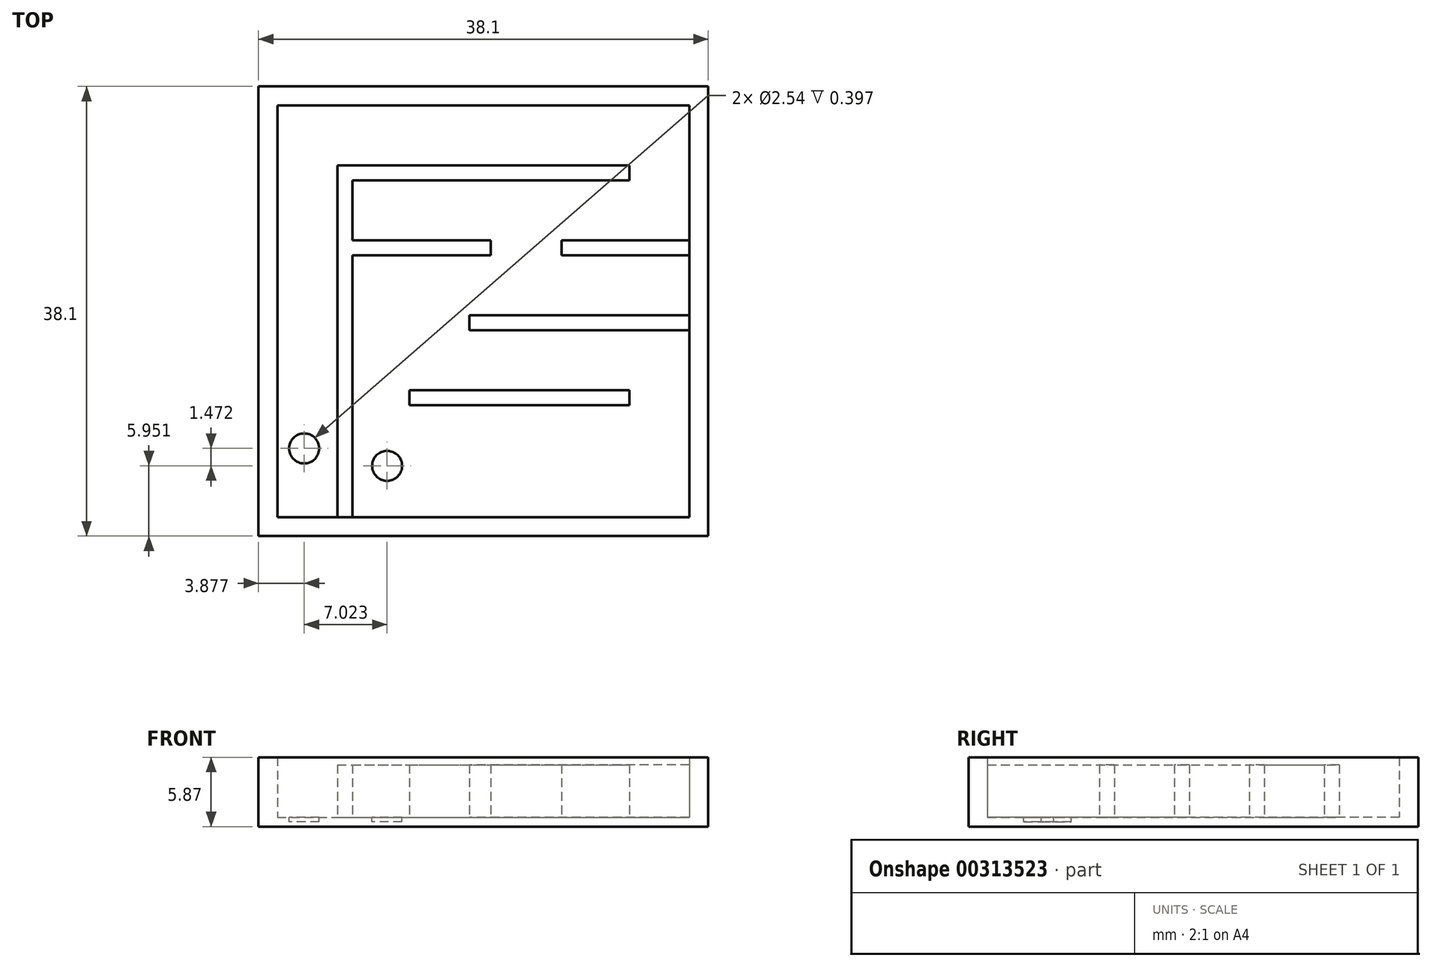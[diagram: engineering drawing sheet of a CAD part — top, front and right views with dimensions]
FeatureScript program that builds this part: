
annotation { "Feature Type Name" : "Feature", "Feature Type Description" : "" }
export const myFeature = defineFeature(function(context is Context, id is Id, definition is map)
    precondition{}
    {
        {
            var Q0;
            Q0=qCreatedBy(makeId("Top.planeOp"),FACE);
            var sketch = newSketch(context, id + "F0", { "sketchPlane" : qUnion([Q0])});
            skLineSegment(sketch, "E0.bottom", {"start": v(-58.63, 60.9) * mm, "end": v(-20.53, 60.9) * mm});
            skLineSegment(sketch, "E0.top", {"start": v(-58.63, 22.8) * mm, "end": v(-20.53, 22.8) * mm});
            skLineSegment(sketch, "E0.left", {"start": v(-58.63, 60.9) * mm, "end": v(-58.63, 22.8) * mm});
            skLineSegment(sketch, "E0.right", {"start": v(-20.53, 60.9) * mm, "end": v(-20.53, 22.8) * mm});
            skSolve(sketch);
        }
        {
            var Q0;
            Q0=makeQuery(id+"F0.imprint","IMPRINT",FACE,{"disambiguationData":[TD([[makeQuery(id+"F0.imprint","IMPRINT",EDGE,{"derivedFrom":sQuery(id+"F0.wireOp",EDGE,"E0.bottom")}),-1.0]])]});
            extrude(context, id + "F1", {"entities" : qUnion([Q0]), "depth" : 0.8 * mm});
        }
        {
            var Q0;
            Q0=makeQuery(id+"F1.opExtrude","CAP_FACE",FACE,{"disambiguationData":[OSD([sQuery(id+"F0.wireOp",EDGE,"E0.bottom"),sQuery(id+"F0.wireOp",EDGE,"E0.top"),sQuery(id+"F0.wireOp",EDGE,"E0.left"),sQuery(id+"F0.wireOp",EDGE,"E0.right")])],"isStart":false});
            var sketch = newSketch(context, id + "F2", { "sketchPlane" : qUnion([Q0])});
            skLineSegment(sketch, "E1.0", {"start": v(-57.03, 59.3) * mm, "end": v(-22.13, 59.3) * mm});
            skLineSegment(sketch, "E1.1", {"start": v(-57.03, 59.3) * mm, "end": v(-57.03, 24.4) * mm});
            skLineSegment(sketch, "E1.2", {"start": v(-57.03, 24.4) * mm, "end": v(-22.13, 24.4) * mm});
            skLineSegment(sketch, "E1.3", {"start": v(-22.13, 59.3) * mm, "end": v(-22.13, 24.4) * mm});
            skSolve(sketch);
        }
        {
            var Q0;
            Q0=makeQuery(id+"F2.imprint","IMPRINT",FACE,{"disambiguationData":[TD([[makeQuery(id+"F2.imprint","IMPRINT",EDGE,{"derivedFrom":sQuery(id+"F2.wireOp",EDGE,"E1.0")}),1.0]])]});
            extrude(context, id + "F3", {"entities" : qUnion([Q0]), "operationType" : NewBodyOperationType.ADD, "depth" : 5.08 * mm});
        }
        {
            var Q0;
            Q0=makeQuery(id+"F1.opExtrude","CAP_FACE",FACE,{"disambiguationData":[OSD([sQuery(id+"F0.wireOp",EDGE,"E0.bottom"),sQuery(id+"F0.wireOp",EDGE,"E0.top"),sQuery(id+"F0.wireOp",EDGE,"E0.left"),sQuery(id+"F0.wireOp",EDGE,"E0.right")])],"isStart":false});
            var sketch = newSketch(context, id + "F4", { "sketchPlane" : qUnion([Q0])});
            skLineSegment(sketch, "E2.bottom", {"start": v(-51.95, 24.4) * mm, "end": v(-50.68, 24.4) * mm});
            skLineSegment(sketch, "E2.top", {"start": v(-51.95, 54.23) * mm, "end": v(-50.68, 54.23) * mm});
            skLineSegment(sketch, "E2.left", {"start": v(-51.95, 24.4) * mm, "end": v(-51.95, 54.23) * mm});
            skLineSegment(sketch, "E2.right", {"start": v(-50.68, 24.4) * mm, "end": v(-50.68, 54.23) * mm});
            skLineSegment(sketch, "E3.bottom", {"start": v(-50.68, 54.23) * mm, "end": v(-27.2, 54.23) * mm});
            skLineSegment(sketch, "E3.top", {"start": v(-50.68, 52.96) * mm, "end": v(-27.2, 52.96) * mm});
            skLineSegment(sketch, "E3.left", {"start": v(-50.68, 54.23) * mm, "end": v(-50.68, 52.96) * mm});
            skLineSegment(sketch, "E3.right", {"start": v(-27.2, 54.23) * mm, "end": v(-27.2, 52.96) * mm});
            skPoint(sketch, "E4.oppositeSnap0", {"position": v(-38.94, 54.23) * mm});
            skLineSegment(sketch, "E4.bottom", {"start": v(-50.68, 47.88) * mm, "end": v(-38.94, 47.88) * mm});
            skLineSegment(sketch, "E4.top", {"start": v(-50.68, 46.6) * mm, "end": v(-38.94, 46.6) * mm});
            skLineSegment(sketch, "E4.left", {"start": v(-50.68, 47.88) * mm, "end": v(-50.68, 46.6) * mm});
            skLineSegment(sketch, "E4.right", {"start": v(-38.94, 47.88) * mm, "end": v(-38.94, 46.6) * mm});
            skLineSegment(sketch, "E5.bottom", {"start": v(-22.13, 47.88) * mm, "end": v(-32.94, 47.88) * mm});
            skLineSegment(sketch, "E5.top", {"start": v(-22.13, 46.6) * mm, "end": v(-32.94, 46.6) * mm});
            skLineSegment(sketch, "E5.left", {"start": v(-22.13, 47.88) * mm, "end": v(-22.13, 46.6) * mm});
            skLineSegment(sketch, "E5.right", {"start": v(-32.94, 47.88) * mm, "end": v(-32.94, 46.6) * mm});
            skLineSegment(sketch, "E6.bottom", {"start": v(-47.12, 46.6) * mm, "end": v(-45.85, 46.6) * mm});
            skLineSegment(sketch, "E6.top", {"start": v(-47.12, 33.9) * mm, "end": v(-45.85, 33.9) * mm});
            skLineSegment(sketch, "E6.left", {"start": v(-47.12, 46.6) * mm, "end": v(-47.12, 33.9) * mm});
            skLineSegment(sketch, "E6.right", {"start": v(-45.85, 46.6) * mm, "end": v(-45.85, 33.9) * mm});
            skLineSegment(sketch, "E7.bottom", {"start": v(-45.85, 33.9) * mm, "end": v(-27.2, 33.9) * mm});
            skLineSegment(sketch, "E7.top", {"start": v(-45.85, 35.18) * mm, "end": v(-27.2, 35.18) * mm});
            skLineSegment(sketch, "E7.left", {"start": v(-45.85, 33.9) * mm, "end": v(-45.85, 35.18) * mm});
            skLineSegment(sketch, "E7.right", {"start": v(-27.2, 33.9) * mm, "end": v(-27.2, 35.18) * mm});
            skLineSegment(sketch, "E8.bottom", {"start": v(-22.13, 41.53) * mm, "end": v(-40.77, 41.53) * mm});
            skLineSegment(sketch, "E8.top", {"start": v(-22.13, 40.26) * mm, "end": v(-40.77, 40.26) * mm});
            skLineSegment(sketch, "E8.left", {"start": v(-22.13, 41.53) * mm, "end": v(-22.13, 40.26) * mm});
            skLineSegment(sketch, "E8.right", {"start": v(-40.77, 41.53) * mm, "end": v(-40.77, 40.26) * mm});
            skSolve(sketch);
        }
        {
            var Q0;
            {var subQ1=sQuery(id+"F4.wireOp",EDGE,"E2.bottom");Q0=makeQuery(id+"F4.imprint","IMPRINT",FACE,{"disambiguationData":[TD([[makeQuery(id+"F4.imprint","IMPRINT",EDGE,{"derivedFrom":subQ1}),1.0]])]});}
            var Q1;
            Q1=makeQuery(id+"F4.imprint","IMPRINT",FACE,{"disambiguationData":[TD([[makeQuery(id+"F4.imprint","IMPRINT",EDGE,{"derivedFrom":sQuery(id+"F4.wireOp",EDGE,"E4.bottom")}),-1.0]])]});
            var Q2;
            Q2=makeQuery(id+"F4.imprint","IMPRINT",FACE,{"disambiguationData":[TD([[makeQuery(id+"F4.imprint","IMPRINT",EDGE,{"derivedFrom":sQuery(id+"F4.wireOp",EDGE,"E6.bottom")}),-1.0]])]});
            var Q3;
            Q3=makeQuery(id+"F4.imprint","IMPRINT",FACE,{"disambiguationData":[TD([[makeQuery(id+"F4.imprint","IMPRINT",EDGE,{"derivedFrom":sQuery(id+"F4.wireOp",EDGE,"E3.bottom")}),-1.0]])]});
            var Q4;
            Q4=makeQuery(id+"F4.imprint","IMPRINT",FACE,{"disambiguationData":[TD([[makeQuery(id+"F4.imprint","IMPRINT",EDGE,{"derivedFrom":sQuery(id+"F4.wireOp",EDGE,"E5.bottom")}),1.0]])]});
            var Q5;
            Q5=makeQuery(id+"F4.imprint","IMPRINT",FACE,{"disambiguationData":[TD([[makeQuery(id+"F4.imprint","IMPRINT",EDGE,{"derivedFrom":sQuery(id+"F4.wireOp",EDGE,"E8.bottom")}),1.0]])]});
            var Q6;
            Q6=makeQuery(id+"F4.imprint","IMPRINT",FACE,{"disambiguationData":[TD([[makeQuery(id+"F4.imprint","IMPRINT",EDGE,{"derivedFrom":sQuery(id+"F4.wireOp",EDGE,"E7.bottom")}),1.0]])]});
            extrude(context, id + "F5", {"entities" : qUnion([Q0, Q1, Q2, Q3, Q4, Q5, Q6]), "operationType" : NewBodyOperationType.ADD, "depth" : 4.44 * mm});
        }
        {
            var Q0;
            Q0=makeQuery(id+"F1.opExtrude","CAP_FACE",FACE,{"disambiguationData":[OSD([sQuery(id+"F0.wireOp",EDGE,"E0.bottom"),sQuery(id+"F0.wireOp",EDGE,"E0.top"),sQuery(id+"F0.wireOp",EDGE,"E0.left"),sQuery(id+"F0.wireOp",EDGE,"E0.right")])],"isStart":false});
            var sketch = newSketch(context, id + "F6", { "sketchPlane" : qUnion([Q0])});
            skCircle(sketch, "E9", {"center": v(-54.75, 30.23) * mm, "radius": 1.27 * mm});
            skCircle(sketch, "E10", {"center": v(-47.73, 28.76) * mm, "radius": 1.27 * mm});
            skSolve(sketch);
        }
        {
            var Q0;
            Q0=makeQuery(id+"F6.imprint","IMPRINT",FACE,{"disambiguationData":[TD([[makeQuery(id+"F6.imprint","IMPRINT",EDGE,{"derivedFrom":sQuery(id+"F6.wireOp",EDGE,"E9")}),1.0]])]});
            var Q1;
            Q1=makeQuery(id+"F6.imprint","IMPRINT",FACE,{"disambiguationData":[TD([[makeQuery(id+"F6.imprint","IMPRINT",EDGE,{"derivedFrom":sQuery(id+"F6.wireOp",EDGE,"E10")}),1.0]])]});
            extrude(context, id + "F7", {"entities" : qUnion([Q0, Q1]), "operationType" : NewBodyOperationType.REMOVE, "oppositeDirection" : true, "depth" : 0.4 * mm});
        }
    });
